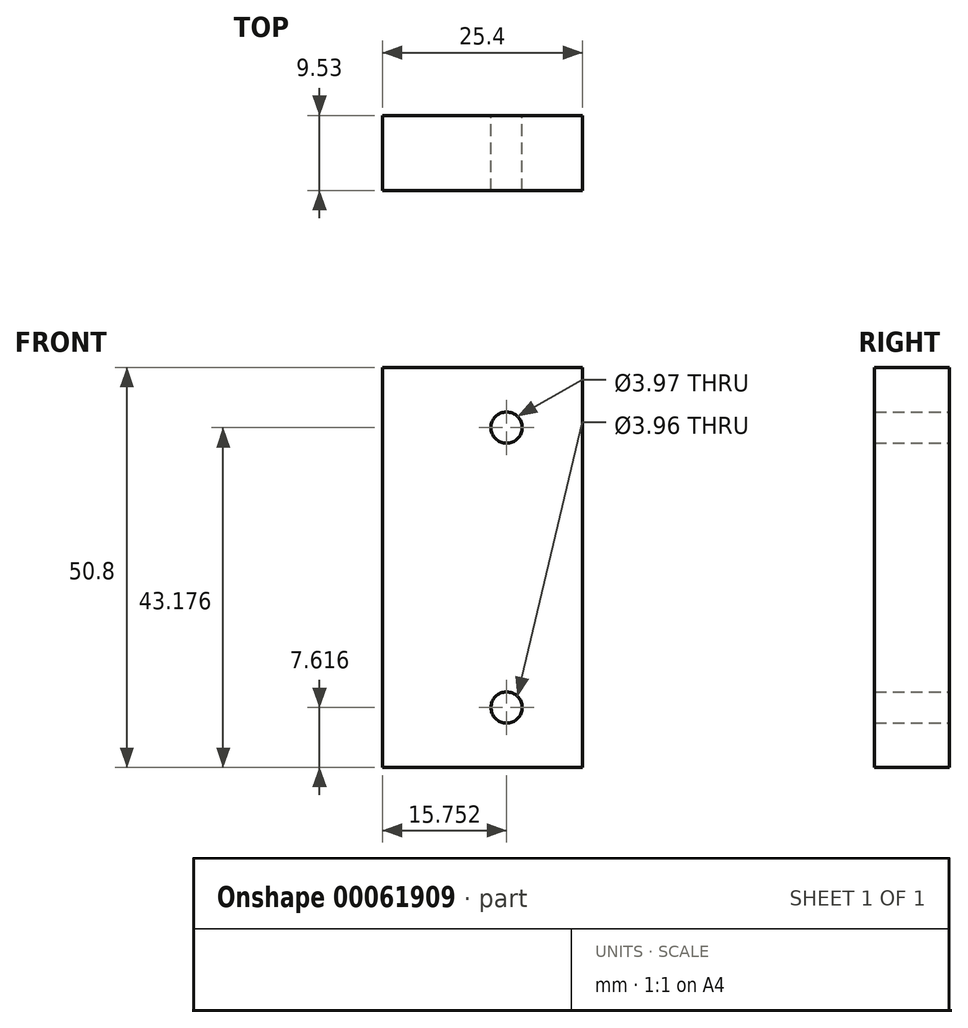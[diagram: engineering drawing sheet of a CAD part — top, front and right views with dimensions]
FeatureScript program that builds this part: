
annotation { "Feature Type Name" : "Feature", "Feature Type Description" : "" }
export const myFeature = defineFeature(function(context is Context, id is Id, definition is map)
    precondition{}
    {
        {
            var Q0;
            Q0=qCreatedBy(makeId("Front.planeOp"),FACE);
            var sketch = newSketch(context, id + "F0", { "sketchPlane" : qUnion([Q0])});
            skLineSegment(sketch, "E0.bottom", {"start": v(-78.05, 33.9) * mm, "end": v(-52.65, 33.9) * mm});
            skLineSegment(sketch, "E0.top", {"start": v(-78.05, -16.9) * mm, "end": v(-52.65, -16.9) * mm});
            skLineSegment(sketch, "E0.left", {"start": v(-78.05, 33.9) * mm, "end": v(-78.05, -16.9) * mm});
            skLineSegment(sketch, "E0.right", {"start": v(-52.65, 33.9) * mm, "end": v(-52.65, -16.9) * mm});
            skLineSegment(sketch, "E1", {"start": v(-62.3, 33.9) * mm, "end": v(-62.3, -16.9) * mm, "construction": true});
            skLineSegment(sketch, "E2", {"start": v(-78.05, -9.28) * mm, "end": v(-52.65, -9.28) * mm, "construction": true});
            skLineSegment(sketch, "E3", {"start": v(-78.05, 26.28) * mm, "end": v(-52.65, 26.28) * mm, "construction": true});
            skPoint(sketch, "E4", {"position": v(-62.3, 26.28) * mm});
            skPoint(sketch, "E5", {"position": v(-62.3, -9.28) * mm});
            skCircle(sketch, "E6", {"center": v(-62.3, 26.28) * mm, "radius": 1.98 * mm});
            skCircle(sketch, "E7", {"center": v(-62.3, -9.28) * mm, "radius": 1.98 * mm});
            skSolve(sketch);
        }
        {
            var Q0;
            Q0=makeQuery(id+"F0.imprint","IMPRINT",FACE,{"disambiguationData":[TD([[makeQuery(id+"F0.imprint","IMPRINT",EDGE,{"derivedFrom":sQuery(id+"F0.wireOp",EDGE,"E0.bottom")}),-1.0]])]});
            extrude(context, id + "F1", {"entities" : qUnion([Q0]), "depth" : 9.52 * mm});
        }
    });
